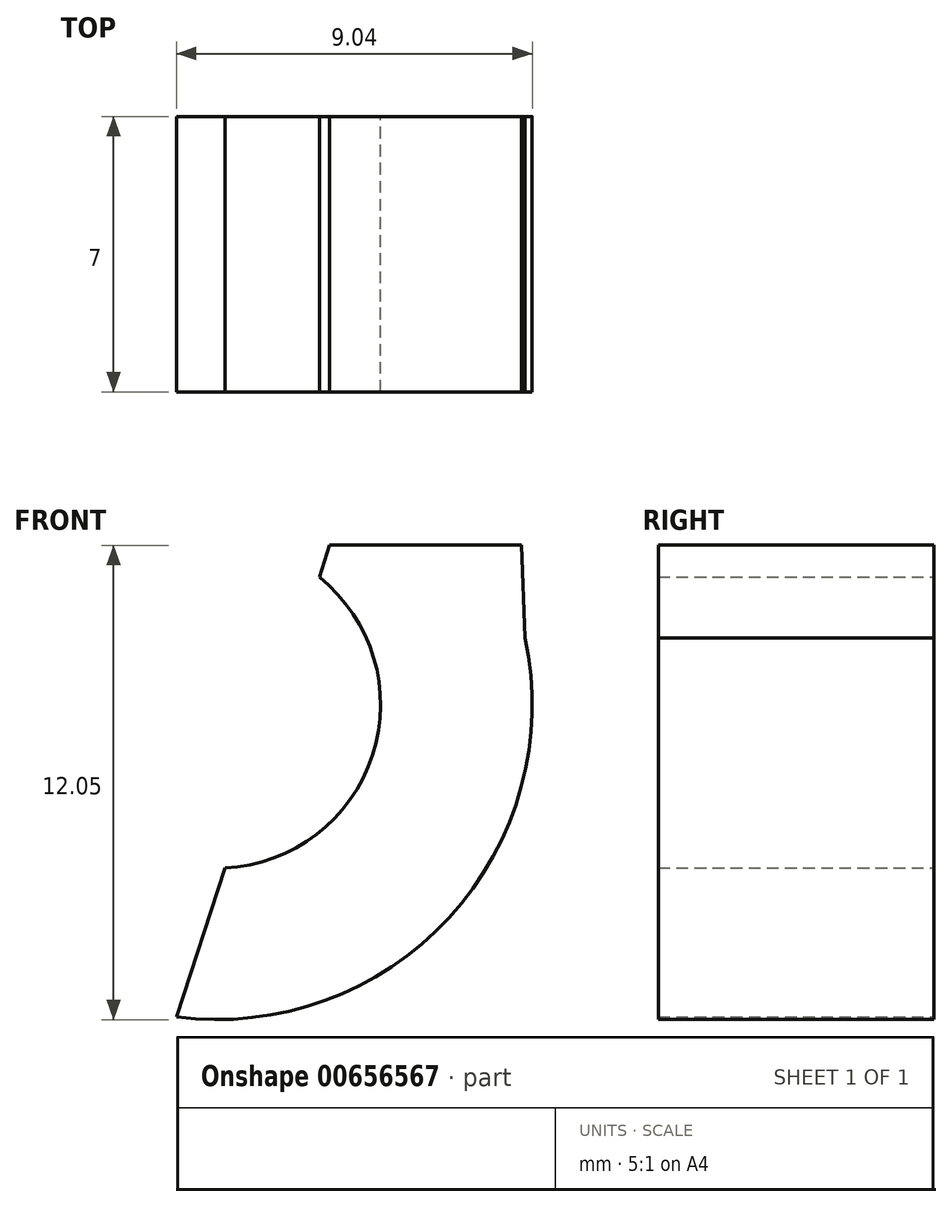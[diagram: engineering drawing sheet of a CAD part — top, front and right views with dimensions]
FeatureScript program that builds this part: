
annotation { "Feature Type Name" : "Feature", "Feature Type Description" : "" }
export const myFeature = defineFeature(function(context is Context, id is Id, definition is map)
    precondition{}
    {
        {
            var Q0;
            Q0=qCreatedBy(makeId("Front.planeOp"),FACE);
            var sketch = newSketch(context, id + "F0", { "sketchPlane" : qUnion([Q0])});
            skCircle(sketch, "E0", {"center": v(-21.21, 21.21) * mm, "radius": 4.15 * mm});
            skCircle(sketch, "E1.MirrorC", {"center": v(21.21, 21.21) * mm, "radius": 4.15 * mm});
            skCircle(sketch, "E2.MirrorC", {"center": v(-21.21, -21.21) * mm, "radius": 4.15 * mm});
            skCircle(sketch, "E3.MirrorC", {"center": v(21.21, -21.21) * mm, "radius": 4.15 * mm});
            skLineSegment(sketch, "E4.0", {"start": v(8.79, 63.66) * mm, "end": v(57.72, 28.1) * mm});
            skLineSegment(sketch, "E4.1", {"start": v(63.18, 11.36) * mm, "end": v(44.67, -46.03) * mm});
            skLineSegment(sketch, "E4.2", {"start": v(30.46, -56.43) * mm, "end": v(-30.25, -56.7) * mm});
            skLineSegment(sketch, "E4.3", {"start": v(-44.56, -46.4) * mm, "end": v(-63.5, 11.05) * mm});
            skLineSegment(sketch, "E4.4", {"start": v(-58.08, 27.88) * mm, "end": v(-8.84, 63.66) * mm});
            skPoint(sketch, "E4.0.midPoint", {"position": v(33.25, 45.89) * mm});
            skLineSegment(sketch, "E5.4", {"start": v(47.54, -5.27) * mm, "end": v(42.66, -20.4) * mm});
            skCircle(sketch, "E6", {"center": v(-0.03, 57.7) * mm, "radius": 2.5 * mm});
            skCircle(sketch, "E7", {"center": v(54.95, 17.7) * mm, "radius": 2.5 * mm});
            skCircle(sketch, "E8", {"center": v(-55.05, 17.7) * mm, "radius": 2.5 * mm});
            skCircle(sketch, "E9", {"center": v(-34, -46.79) * mm, "radius": 2.5 * mm});
            skCircle(sketch, "E10", {"center": v(33.96, -46.92) * mm, "radius": 2.5 * mm});
            skPoint(sketch, "E11.visualSharp", {"position": v(-0.03, 70.06) * mm});
            skArc(sketch, "E11.filletArc", {"start": v(8.79, 63.66) * mm, "mid": v(-0.03, 66.52) * mm, "end": v(-8.84, 63.66) * mm});
            skPoint(sketch, "E12.visualSharp", {"position": v(-66.94, 21.45) * mm});
            skArc(sketch, "E12.filletArc", {"start": v(-58.08, 27.88) * mm, "mid": v(-63.54, 20.35) * mm, "end": v(-63.5, 11.05) * mm});
            skPoint(sketch, "E13.visualSharp", {"position": v(-41.15, -56.74) * mm});
            skArc(sketch, "E13.filletArc", {"start": v(-44.56, -46.4) * mm, "mid": v(-39.08, -53.87) * mm, "end": v(-30.25, -56.7) * mm});
            skPoint(sketch, "E14.visualSharp", {"position": v(41.34, -56.38) * mm});
            skArc(sketch, "E14.filletArc", {"start": v(30.46, -56.43) * mm, "mid": v(39.26, -53.53) * mm, "end": v(44.67, -46.03) * mm});
            skPoint(sketch, "E15.visualSharp", {"position": v(66.52, 21.71) * mm});
            skArc(sketch, "E15.filletArc", {"start": v(63.18, 11.36) * mm, "mid": v(63.17, 20.62) * mm, "end": v(57.72, 28.1) * mm});
            skArc(sketch, "E16", {"start": v(-13.24, -21.8) * mm, "mid": v(-15.87, -15.26) * mm, "end": v(-22.65, -13.34) * mm});
            skArc(sketch, "E17", {"start": v(26, -14.8) * mm, "mid": v(18.65, -13.64) * mm, "end": v(13.52, -19.02) * mm});
            skArc(sketch, "E18", {"start": v(13.22, 21.5) * mm, "mid": v(18, 13.88) * mm, "end": v(26.86, 15.55) * mm});
            skArc(sketch, "E19", {"start": v(-26.3, 15.03) * mm, "mid": v(-17.04, 14.39) * mm, "end": v(-13.4, 22.91) * mm});
            skLineSegment(sketch, "E20", {"start": v(26, -14.8) * mm, "end": v(36.5, -22.42) * mm});
            skLineSegment(sketch, "E21.trimOffspring", {"start": v(-45.56, -11.09) * mm, "end": v(-47.7, -4.62) * mm});
            skLineSegment(sketch, "E22.trimOffspring", {"start": v(4.18, -46.76) * mm, "end": v(-4.27, -46.8) * mm});
            skArc(sketch, "E23", {"start": v(39.21, 21.25) * mm, "mid": v(39.65, 12.6) * mm, "end": v(44.5, 5.42) * mm});
            skArc(sketch, "E24", {"start": v(-11.33, 44.27) * mm, "mid": v(-0.1, 40.14) * mm, "end": v(11.17, 44.18) * mm});
            skArc(sketch, "E25", {"start": v(-44.8, 6.03) * mm, "mid": v(-40.25, 12.95) * mm, "end": v(-39.91, 21.22) * mm});
            skLineSegment(sketch, "E26", {"start": v(-26.3, 15.03) * mm, "end": v(-37.2, 23) * mm});
            skLineSegment(sketch, "E27", {"start": v(14, 42.78) * mm, "end": v(13.22, 21.5) * mm});
            skLineSegment(sketch, "E28", {"start": v(36.46, 23) * mm, "end": v(26.86, 15.55) * mm});
            skLineSegment(sketch, "E29", {"start": v(-14.18, 42.88) * mm, "end": v(-13.4, 22.91) * mm});
            skLineSegment(sketch, "E30", {"start": v(-14.29, -36.06) * mm, "end": v(-13.24, -21.8) * mm});
            skLineSegment(sketch, "E31", {"start": v(-32.33, -17.24) * mm, "end": v(-22.65, -13.34) * mm});
            skLineSegment(sketch, "E32", {"start": v(14.13, -36.41) * mm, "end": v(13.52, -19.02) * mm});
            skPoint(sketch, "E33.visualSharp", {"position": v(14.5, -46.72) * mm});
            skArc(sketch, "E33.filletArc", {"start": v(4.18, -46.76) * mm, "mid": v(11.35, -43.7) * mm, "end": v(14.13, -36.41) * mm});
            skPoint(sketch, "E34.visualSharp", {"position": v(-15.09, -46.85) * mm});
            skArc(sketch, "E34.filletArc", {"start": v(-14.29, -36.06) * mm, "mid": v(-11.63, -43.62) * mm, "end": v(-4.27, -46.8) * mm});
            skPoint(sketch, "E35.visualSharp", {"position": v(-42.22, -21.21) * mm});
            skArc(sketch, "E35.filletArc", {"start": v(-45.56, -11.09) * mm, "mid": v(-40.27, -17.03) * mm, "end": v(-32.33, -17.24) * mm});
            skPoint(sketch, "E36.visualSharp", {"position": v(-42.5, 26.88) * mm});
            skArc(sketch, "E36.filletArc", {"start": v(-37.2, 23) * mm, "mid": v(-39.18, 23.05) * mm, "end": v(-39.91, 21.22) * mm});
            skPoint(sketch, "E37.visualSharp", {"position": v(-14.36, 47.56) * mm});
            skArc(sketch, "E37.filletArc", {"start": v(-11.33, 44.27) * mm, "mid": v(-13.2, 44.5) * mm, "end": v(-14.18, 42.88) * mm});
            skPoint(sketch, "E38.visualSharp", {"position": v(14.17, 47.37) * mm});
            skArc(sketch, "E38.filletArc", {"start": v(14, 42.78) * mm, "mid": v(13.04, 44.4) * mm, "end": v(11.17, 44.18) * mm});
            skPoint(sketch, "E39.visualSharp", {"position": v(41.96, 27.27) * mm});
            skArc(sketch, "E39.filletArc", {"start": v(39.21, 21.25) * mm, "mid": v(38.45, 23.1) * mm, "end": v(36.46, 23) * mm});
            skPoint(sketch, "E40.visualSharp", {"position": v(50, 2.35) * mm});
            skArc(sketch, "E40.filletArc", {"start": v(47.54, -5.27) * mm, "mid": v(47.64, 0.53) * mm, "end": v(44.5, 5.42) * mm});
            skPoint(sketch, "E41.visualSharp", {"position": v(40.96, -25.66) * mm});
            skArc(sketch, "E41.filletArc", {"start": v(36.5, -22.42) * mm, "mid": v(40.09, -22.98) * mm, "end": v(42.66, -20.4) * mm});
            skPoint(sketch, "E42.visualSharp", {"position": v(-50.18, 2.94) * mm});
            skArc(sketch, "E42.filletArc", {"start": v(-44.8, 6.03) * mm, "mid": v(-47.84, 1.14) * mm, "end": v(-47.7, -4.62) * mm});
            skLineSegment(sketch, "E43", {"start": v(33.96, -46.92) * mm, "end": v(-55.05, 17.7) * mm, "construction": true});
            skLineSegment(sketch, "E44", {"start": v(-0.03, 57.7) * mm, "end": v(33.96, -46.92) * mm, "construction": true});
            skLineSegment(sketch, "E45", {"start": v(54.95, 17.7) * mm, "end": v(-55.05, 17.7) * mm, "construction": true});
            skLineSegment(sketch, "E46", {"start": v(113.98, 67.67) * mm, "end": v(113.98, -63.45) * mm});
            skCircle(sketch, "E47.MirrorC", {"center": v(227.99, 57.7) * mm, "radius": 2.5 * mm});
            skCircle(sketch, "E48.MirrorC", {"center": v(206.75, 21.21) * mm, "radius": 4.15 * mm});
            skCircle(sketch, "E49.MirrorC", {"center": v(173.01, 17.7) * mm, "radius": 2.5 * mm});
            skCircle(sketch, "E50.MirrorC", {"center": v(206.75, -21.21) * mm, "radius": 4.15 * mm});
            skCircle(sketch, "E51.MirrorC", {"center": v(194, -46.92) * mm, "radius": 2.5 * mm});
            skCircle(sketch, "E52.MirrorC", {"center": v(261.95, -46.79) * mm, "radius": 2.5 * mm});
            skCircle(sketch, "E53.MirrorC", {"center": v(249.17, -21.21) * mm, "radius": 4.15 * mm});
            skCircle(sketch, "E54.MirrorC", {"center": v(249.17, 21.21) * mm, "radius": 4.15 * mm});
            skCircle(sketch, "E55.cCircle", {"center": v(0, 0) * mm, "radius": 25.26 * mm, "construction": true});
            skLineSegment(sketch, "E55.0", {"start": v(-18.36, 25.26) * mm, "end": v(18.36, 25.26) * mm});
            skLineSegment(sketch, "E55.1", {"start": v(18.36, 25.26) * mm, "end": v(29.7, -9.65) * mm});
            skLineSegment(sketch, "E55.2", {"start": v(29.7, -9.65) * mm, "end": v(0, -31.23) * mm});
            skLineSegment(sketch, "E55.3", {"start": v(0, -31.23) * mm, "end": v(-29.7, -9.65) * mm});
            skLineSegment(sketch, "E55.4", {"start": v(-29.7, -9.65) * mm, "end": v(-18.36, 25.26) * mm});
            skPoint(sketch, "E55.0.midPoint", {"position": v(0, 25.26) * mm});
            skSolve(sketch);
        }
        {
            var Q0;
            Q0=makeQuery(id+"F0.imprint","IMPRINT",FACE,{"disambiguationData":[TD([[makeQuery(id+"F0.imprint","IMPRINT",EDGE,{"derivedFrom":sQuery(id+"F0.wireOp",EDGE,"E0")}),-1.0]])]});
            extrude(context, id + "F1", {"entities" : qUnion([Q0]), "depth" : 7 * mm, "offsetDistance" : 25 * mm});
        }
    });
